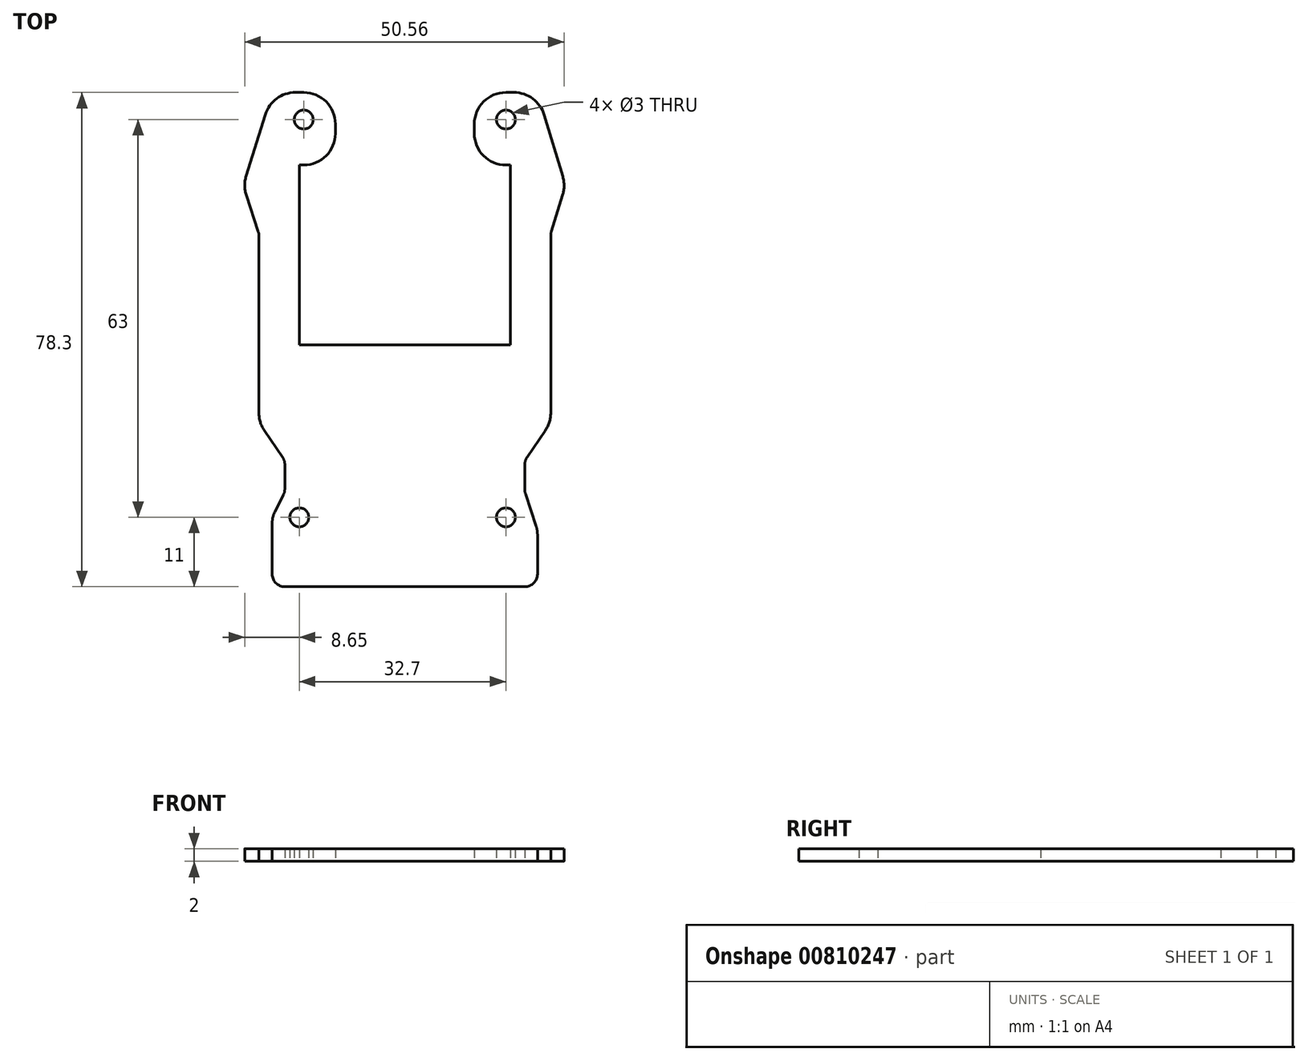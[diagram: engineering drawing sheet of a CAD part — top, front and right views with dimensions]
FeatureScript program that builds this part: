
annotation { "Feature Type Name" : "Feature", "Feature Type Description" : "" }
export const myFeature = defineFeature(function(context is Context, id is Id, definition is map)
    precondition{}
    {
        {
            var Q0;
            Q0=qCreatedBy(makeId("Top.planeOp"),FACE);
            var sketch = newSketch(context, id + "F0", { "sketchPlane" : qUnion([Q0])});
            skLineSegment(sketch, "E0", {"start": v(-16.7, -0.85) * mm, "end": v(-16.7, 27.65) * mm});
            skLineSegment(sketch, "E1", {"start": v(-16.7, 27.65) * mm, "end": v(-11, 27.65) * mm});
            skLineSegment(sketch, "E2", {"start": v(-11, 27.65) * mm, "end": v(-11, 39.15) * mm});
            skLineSegment(sketch, "E3", {"start": v(-21, 39.15) * mm, "end": v(-25.6, 24.35) * mm});
            skLineSegment(sketch, "E4", {"start": v(-25.6, 24.35) * mm, "end": v(-23.1, 16.82) * mm});
            skLineSegment(sketch, "E5", {"start": v(-23.1, 16.82) * mm, "end": v(-23.1, -13.15) * mm});
            skLineSegment(sketch, "E6", {"start": v(-19, -24.15) * mm, "end": v(-21, -28.15) * mm});
            skLineSegment(sketch, "E7", {"start": v(-21, -28.15) * mm, "end": v(-21, -39.15) * mm});
            skLineSegment(sketch, "E8", {"start": v(-21, -39.15) * mm, "end": v(21, -39.15) * mm});
            skLineSegment(sketch, "E9", {"start": v(-19, -24.15) * mm, "end": v(-19, -19.15) * mm});
            skLineSegment(sketch, "E10", {"start": v(-19, -19.15) * mm, "end": v(-23.1, -13.15) * mm});
            skLineSegment(sketch, "E11", {"start": v(-16.7, -0.85) * mm, "end": v(16.7, -0.85) * mm});
            skLineSegment(sketch, "E12", {"start": v(16.7, -0.85) * mm, "end": v(16.7, 27.65) * mm});
            skLineSegment(sketch, "E13", {"start": v(16.7, 27.65) * mm, "end": v(11, 27.65) * mm});
            skLineSegment(sketch, "E14", {"start": v(11, 27.65) * mm, "end": v(11, 39.15) * mm});
            skLineSegment(sketch, "E15", {"start": v(11, 39.15) * mm, "end": v(21, 39.15) * mm});
            skLineSegment(sketch, "E16", {"start": v(21, 39.15) * mm, "end": v(25.44, 24.35) * mm});
            skLineSegment(sketch, "E17", {"start": v(25.44, 24.35) * mm, "end": v(23.1, 16.82) * mm});
            skLineSegment(sketch, "E18", {"start": v(23.1, 16.82) * mm, "end": v(23.1, -13.15) * mm});
            skLineSegment(sketch, "E19", {"start": v(23.1, -13.15) * mm, "end": v(19, -19.15) * mm});
            skLineSegment(sketch, "E20", {"start": v(19, -19.15) * mm, "end": v(19, -24.15) * mm});
            skLineSegment(sketch, "E21", {"start": v(19, -24.15) * mm, "end": v(21, -30.17) * mm});
            skLineSegment(sketch, "E22", {"start": v(21, -30.17) * mm, "end": v(21, -39.15) * mm});
            skLineSegment(sketch, "E23", {"start": v(-21, 39.15) * mm, "end": v(-11, 39.15) * mm});
            skCircle(sketch, "E24", {"center": v(16, 34.85) * mm, "radius": 1.5 * mm});
            skCircle(sketch, "E25", {"center": v(-16, 34.85) * mm, "radius": 1.5 * mm});
            skCircle(sketch, "E26", {"center": v(-16.7, -28.15) * mm, "radius": 1.5 * mm});
            skCircle(sketch, "E27", {"center": v(16, -28.15) * mm, "radius": 1.5 * mm});
            skSolve(sketch);
        }
        {
            var Q0;
            Q0 = qSketchRegion(id + "F0", true);
            extrude(context, id + "F1", {"entities" : qUnion([Q0]), "depth" : 2 * mm, "offsetDistance" : 25 * mm});
        }
        {
            var Q0;
            Q0=makeQuery(id+"F1.opExtrude","SWEPT_EDGE",EDGE,{"disambiguationData":[OSD([sQuery(id+"F0.wireOp",EDGE,"E1"),sQuery(id+"F0.wireOp",EDGE,"E2")])]});
            var Q1;
            Q1=makeQuery(id+"F1.opExtrude","SWEPT_EDGE",EDGE,{"disambiguationData":[OSD([sQuery(id+"F0.wireOp",EDGE,"E13"),sQuery(id+"F0.wireOp",EDGE,"E14")])]});
            var Q2;
            Q2=makeQuery(id+"F1.opExtrude","SWEPT_EDGE",EDGE,{"disambiguationData":[OSD([sQuery(id+"F0.wireOp",EDGE,"E14"),sQuery(id+"F0.wireOp",EDGE,"E15")])]});
            var Q3;
            Q3=makeQuery(id+"F1.opExtrude","SWEPT_EDGE",EDGE,{"disambiguationData":[OSD([sQuery(id+"F0.wireOp",EDGE,"E15"),sQuery(id+"F0.wireOp",EDGE,"E16")])]});
            var Q4;
            Q4=makeQuery(id+"F1.opExtrude","SWEPT_EDGE",EDGE,{"disambiguationData":[OSD([sQuery(id+"F0.wireOp",EDGE,"E2"),sQuery(id+"F0.wireOp",EDGE,"E23")])]});
            var Q5;
            Q5=makeQuery(id+"F1.opExtrude","SWEPT_EDGE",EDGE,{"disambiguationData":[OSD([sQuery(id+"F0.wireOp",EDGE,"E3"),sQuery(id+"F0.wireOp",EDGE,"E23")])]});
            var Q6;
            Q6=makeQuery(id+"F1.opExtrude","SWEPT_EDGE",EDGE,{"disambiguationData":[OSD([sQuery(id+"F0.wireOp",EDGE,"E3"),sQuery(id+"F0.wireOp",EDGE,"E4")])]});
            var Q7;
            Q7=makeQuery(id+"F1.opExtrude","SWEPT_EDGE",EDGE,{"disambiguationData":[OSD([sQuery(id+"F0.wireOp",EDGE,"E16"),sQuery(id+"F0.wireOp",EDGE,"E17")])]});
            var Q8;
            Q8=makeQuery(id+"F1.opExtrude","SWEPT_EDGE",EDGE,{"disambiguationData":[OSD([sQuery(id+"F0.wireOp",EDGE,"E18"),sQuery(id+"F0.wireOp",EDGE,"E19")])]});
            var Q9;
            Q9=makeQuery(id+"F1.opExtrude","SWEPT_EDGE",EDGE,{"disambiguationData":[OSD([sQuery(id+"F0.wireOp",EDGE,"E5"),sQuery(id+"F0.wireOp",EDGE,"E10")])]});
            fillet(context, id + "F2", {"entities" : qUnion([Q0, Q1, Q2, Q3, Q4, Q5, Q6, Q7, Q8, Q9]), "radius" : 5 * mm, "tangentPropagation" : true, "allowEdgeOverflow" : false});
        }
        {
            var Q0;
            Q0=makeQuery(id+"F1.opExtrude","SWEPT_EDGE",EDGE,{"disambiguationData":[OSD([sQuery(id+"F0.wireOp",EDGE,"E17"),sQuery(id+"F0.wireOp",EDGE,"E18")])]});
            var Q1;
            Q1=makeQuery(id+"F1.opExtrude","SWEPT_EDGE",EDGE,{"disambiguationData":[OSD([sQuery(id+"F0.wireOp",EDGE,"E4"),sQuery(id+"F0.wireOp",EDGE,"E5")])]});
            var Q2;
            Q2=makeQuery(id+"F1.opExtrude","SWEPT_EDGE",EDGE,{"disambiguationData":[OSD([sQuery(id+"F0.wireOp",EDGE,"E9"),sQuery(id+"F0.wireOp",EDGE,"E10")])]});
            var Q3;
            Q3=makeQuery(id+"F1.opExtrude","SWEPT_EDGE",EDGE,{"disambiguationData":[OSD([sQuery(id+"F0.wireOp",EDGE,"E6"),sQuery(id+"F0.wireOp",EDGE,"E9")])]});
            var Q4;
            Q4=makeQuery(id+"F1.opExtrude","SWEPT_EDGE",EDGE,{"disambiguationData":[OSD([sQuery(id+"F0.wireOp",EDGE,"E19"),sQuery(id+"F0.wireOp",EDGE,"E20")])]});
            var Q5;
            Q5=makeQuery(id+"F1.opExtrude","SWEPT_EDGE",EDGE,{"disambiguationData":[OSD([sQuery(id+"F0.wireOp",EDGE,"E20"),sQuery(id+"F0.wireOp",EDGE,"E21")])]});
            var Q6;
            Q6=makeQuery(id+"F1.opExtrude","SWEPT_EDGE",EDGE,{"disambiguationData":[OSD([sQuery(id+"F0.wireOp",EDGE,"E8"),sQuery(id+"F0.wireOp",EDGE,"E22")])]});
            var Q7;
            Q7=makeQuery(id+"F1.opExtrude","SWEPT_EDGE",EDGE,{"disambiguationData":[OSD([sQuery(id+"F0.wireOp",EDGE,"E7"),sQuery(id+"F0.wireOp",EDGE,"E8")])]});
            fillet(context, id + "F3", {"entities" : qUnion([Q0, Q1, Q2, Q3, Q4, Q5, Q6, Q7]), "radius" : 2 * mm, "tangentPropagation" : true, "allowEdgeOverflow" : false});
        }
        {
            var Q0;
            Q0=makeQuery(id+"F1.opExtrude","SWEPT_EDGE",EDGE,{"disambiguationData":[OSD([sQuery(id+"F0.wireOp",EDGE,"E6"),sQuery(id+"F0.wireOp",EDGE,"E7")])]});
            var Q1;
            Q1=makeQuery(id+"F1.opExtrude","SWEPT_EDGE",EDGE,{"disambiguationData":[OSD([sQuery(id+"F0.wireOp",EDGE,"E21"),sQuery(id+"F0.wireOp",EDGE,"E22")])]});
            fillet(context, id + "F4", {"entities" : qUnion([Q0, Q1]), "radius" : 4 * mm, "tangentPropagation" : true, "allowEdgeOverflow" : false});
        }
    });
